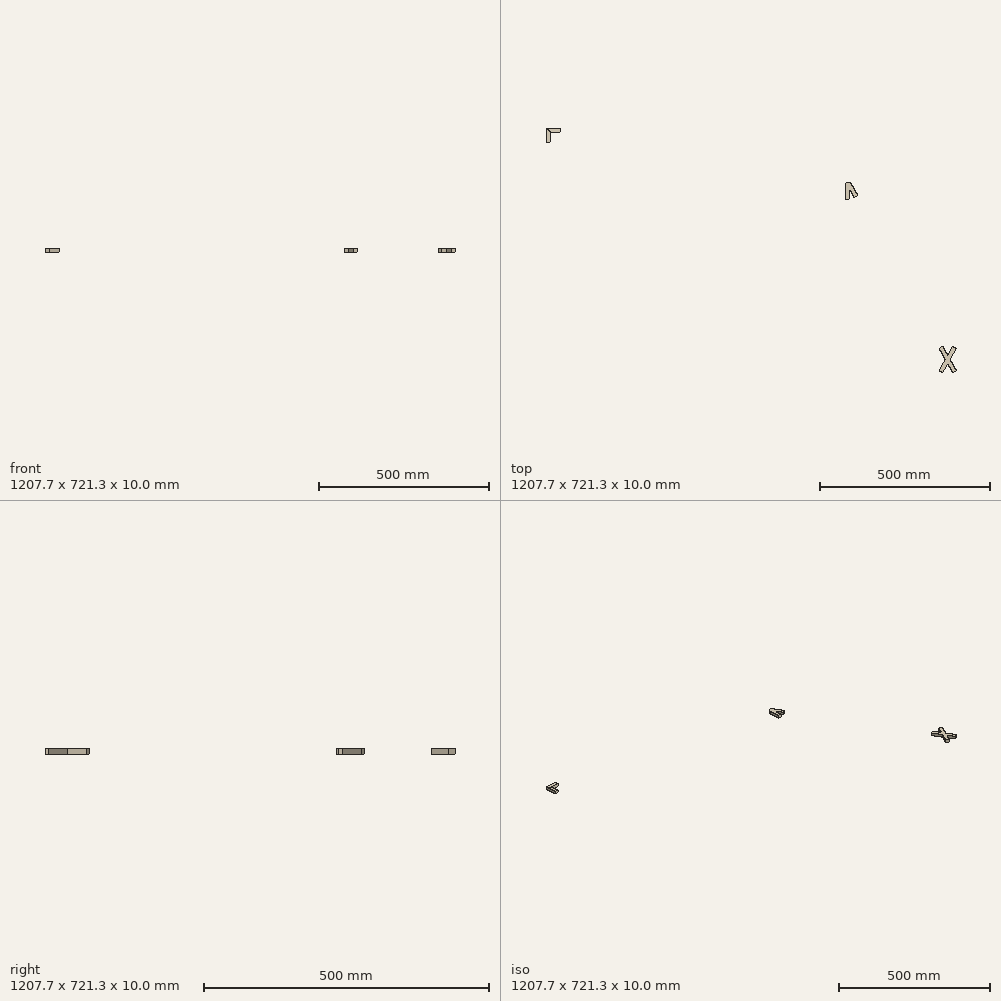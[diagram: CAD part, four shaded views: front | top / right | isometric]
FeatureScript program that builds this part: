
annotation { "Feature Type Name" : "Feature", "Feature Type Description" : "" }
export const myFeature = defineFeature(function(context is Context, id is Id, definition is map)
    precondition{}
    {
        {
            assignVariable(context, id + "F0", {"name" : "arm_height", "anyValue" : 10});
        }
        {
            var Q0;
            Q0=qCreatedBy(makeId("Top.planeOp"),FACE);
            var sketch = newSketch(context, id + "F1", { "sketchPlane" : qUnion([Q0])});
            skLineSegment(sketch, "E0.bottom", {"start": v(0, 0) * mm, "end": v(12.5, 0) * mm});
            skLineSegment(sketch, "E0.top", {"start": v(0, -1006) * mm, "end": v(12.5, -1006) * mm});
            skLineSegment(sketch, "E0.left", {"start": v(0, 0) * mm, "end": v(0, -1006) * mm});
            skLineSegment(sketch, "E0.right", {"start": v(12.5, 0) * mm, "end": v(12.5, -1006) * mm});
            skLineSegment(sketch, "E1.bottom", {"start": v(592.5, 0) * mm, "end": v(605, 0) * mm});
            skLineSegment(sketch, "E1.top", {"start": v(592.5, -1006) * mm, "end": v(605, -1006) * mm});
            skLineSegment(sketch, "E1.left", {"start": v(592.5, 0) * mm, "end": v(592.5, -1006) * mm});
            skLineSegment(sketch, "E1.right", {"start": v(605, 0) * mm, "end": v(605, -1006) * mm});
            skSolve(sketch);
        }
        {
            var Q0;
            Q0=qCreatedBy(makeId("Top.planeOp"),FACE);
            var sketch = newSketch(context, id + "F2", { "sketchPlane" : qUnion([Q0])});
            skLineSegment(sketch, "E2", {"start": v(0, -30) * mm, "end": v(0, 9.55) * mm});
            skLineSegment(sketch, "E3", {"start": v(18.72, 14.45) * mm, "end": v(38.1, -20.02) * mm});
            skLineSegment(sketch, "E4", {"start": v(38.1, -20.02) * mm, "end": v(27.2, -26.15) * mm});
            skLineSegment(sketch, "E5", {"start": v(27.2, -26.15) * mm, "end": v(12.5, 0) * mm});
            skLineSegment(sketch, "E6", {"start": v(12.5, 0) * mm, "end": v(12.5, -30) * mm});
            skLineSegment(sketch, "E7", {"start": v(12.5, -30) * mm, "end": v(0, -30) * mm});
            skLineSegment(sketch, "E8.0.0", {"start": v(0, 0) * mm, "end": v(0, -1006) * mm, "construction": true});
            skLineSegment(sketch, "E8.0.1", {"start": v(0, -1006) * mm, "end": v(12.5, -1006) * mm, "construction": true});
            skLineSegment(sketch, "E8.0.2", {"start": v(12.5, -1006) * mm, "end": v(12.5, 0) * mm, "construction": true});
            skLineSegment(sketch, "E8.0.3", {"start": v(12.5, 0) * mm, "end": v(0, 0) * mm, "construction": true});
            skLineSegment(sketch, "E9.0.0", {"start": v(592.5, 0) * mm, "end": v(592.5, -1006) * mm, "construction": true});
            skLineSegment(sketch, "E9.0.1", {"start": v(592.5, -1006) * mm, "end": v(605, -1006) * mm, "construction": true});
            skLineSegment(sketch, "E9.0.2", {"start": v(605, -1006) * mm, "end": v(605, 0) * mm, "construction": true});
            skLineSegment(sketch, "E9.0.3", {"start": v(605, 0) * mm, "end": v(592.5, 0) * mm, "construction": true});
            skLineSegment(sketch, "E10", {"start": v(12.5, 0) * mm, "end": v(581.6, -1012.13) * mm, "construction": true});
            skLineSegment(sketch, "E11", {"start": v(592.5, -1006) * mm, "end": v(23.4, 6.13) * mm, "construction": true});
            skLineSegment(sketch, "E12", {"start": v(23.4, 6.13) * mm, "end": v(12.5, 0) * mm, "construction": true});
            skLineSegment(sketch, "E13", {"start": v(581.6, -1012.13) * mm, "end": v(592.5, -1006) * mm, "construction": true});
            skLineSegment(sketch, "E14", {"start": v(592.5, 0) * mm, "end": v(12.5, 0) * mm, "construction": true});
            skPoint(sketch, "E15", {"position": v(302.5, 0) * mm});
            skLineSegment(sketch, "E16", {"start": v(302.5, 0) * mm, "end": v(302.5, -1006) * mm, "construction": true});
            skLineSegment(sketch, "E17.MirrorCS", {"start": v(23.4, -1012.13) * mm, "end": v(12.5, -1006) * mm, "construction": true});
            skLineSegment(sketch, "E18.MirrorCS", {"start": v(581.6, 6.13) * mm, "end": v(592.5, 0) * mm, "construction": true});
            skLineSegment(sketch, "E19.MirrorCS", {"start": v(592.5, 0) * mm, "end": v(23.4, -1012.13) * mm, "construction": true});
            skLineSegment(sketch, "E20.MirrorCS", {"start": v(12.5, -1006) * mm, "end": v(581.6, 6.13) * mm, "construction": true});
            skPoint(sketch, "E21.visualSharp", {"position": v(0, 47.73) * mm});
            skArc(sketch, "E21.filletArc", {"start": v(18.72, 14.45) * mm, "mid": v(7.47, 19.22) * mm, "end": v(0, 9.55) * mm});
            skSolve(sketch);
        }
        {
            var Q0;
            Q0=qCreatedBy(makeId("Top.planeOp"),FACE);
            var sketch = newSketch(context, id + "F3", { "sketchPlane" : qUnion([Q0])});
            skLineSegment(sketch, "E22.0", {"start": v(592.5, -1006) * mm, "end": v(23.4, 6.13) * mm, "construction": true});
            skLineSegment(sketch, "E23.0", {"start": v(12.5, 0) * mm, "end": v(581.6, -1012.13) * mm, "construction": true});
            skLineSegment(sketch, "E24.0", {"start": v(12.5, -1006) * mm, "end": v(581.6, 6.13) * mm, "construction": true});
            skLineSegment(sketch, "E25.0", {"start": v(592.5, 0) * mm, "end": v(23.4, -1012.13) * mm, "construction": true});
            skLineSegment(sketch, "E26", {"start": v(276.9, -470.22) * mm, "end": v(287.8, -464.1) * mm});
            skLineSegment(sketch, "E27", {"start": v(287.8, -464.1) * mm, "end": v(302.5, -490.25) * mm});
            skLineSegment(sketch, "E28", {"start": v(302.5, -490.25) * mm, "end": v(317.2, -464.1) * mm});
            skLineSegment(sketch, "E29", {"start": v(317.2, -464.1) * mm, "end": v(328.1, -470.22) * mm});
            skLineSegment(sketch, "E30", {"start": v(328.1, -470.22) * mm, "end": v(309.67, -503) * mm});
            skLineSegment(sketch, "E31", {"start": v(309.67, -503) * mm, "end": v(328.1, -535.78) * mm});
            skLineSegment(sketch, "E32", {"start": v(328.1, -535.78) * mm, "end": v(317.2, -541.9) * mm});
            skLineSegment(sketch, "E33", {"start": v(317.2, -541.9) * mm, "end": v(302.5, -515.75) * mm});
            skLineSegment(sketch, "E34", {"start": v(302.5, -515.75) * mm, "end": v(287.8, -541.9) * mm});
            skLineSegment(sketch, "E35", {"start": v(287.8, -541.9) * mm, "end": v(276.9, -535.78) * mm});
            skLineSegment(sketch, "E36", {"start": v(276.9, -535.78) * mm, "end": v(295.33, -503) * mm});
            skLineSegment(sketch, "E37", {"start": v(295.33, -503) * mm, "end": v(276.9, -470.22) * mm});
            skSolve(sketch);
        }
        {
            var Q0;
            Q0=makeQuery(id+"F2.imprint","IMPRINT",FACE,{"disambiguationData":[TD([[makeQuery(id+"F2.imprint","IMPRINT",EDGE,{"derivedFrom":sQuery(id+"F2.wireOp",EDGE,"E2")}),-1.0]])]});
            var Q1;
            Q1=makeQuery(id+"F3.imprint","IMPRINT",FACE,{"disambiguationData":[TD([[makeQuery(id+"F3.imprint","IMPRINT",EDGE,{"derivedFrom":sQuery(id+"F3.wireOp",EDGE,"E26")}),-1.0]])]});
            extrude(context, id + "F4", {"entities" : qUnion([Q0, Q1]), "depth" : (getVariable(context, 'arm_height')) * mm, "offsetDistance" : 25 * mm});
        }
        {
            var Q0;
            Q0=qCreatedBy(makeId("Top.planeOp"),FACE);
            var sketch = newSketch(context, id + "F5", { "sketchPlane" : qUnion([Q0])});
            skLineSegment(sketch, "E38", {"start": v(-879.62, 179.38) * mm, "end": v(-879.62, 136.88) * mm});
            skLineSegment(sketch, "E39", {"start": v(-879.62, 136.88) * mm, "end": v(-867.12, 136.88) * mm});
            skLineSegment(sketch, "E40", {"start": v(-867.12, 136.88) * mm, "end": v(-867.12, 166.88) * mm});
            skLineSegment(sketch, "E41", {"start": v(-867.12, 166.88) * mm, "end": v(-879.62, 179.38) * mm});
            skSolve(sketch);
        }
        {
            var Q0;
            Q0=makeQuery(id+"F5.imprint","IMPRINT",FACE,{"disambiguationData":[TD([[makeQuery(id+"F5.imprint","IMPRINT",EDGE,{"derivedFrom":sQuery(id+"F5.wireOp",EDGE,"E38")}),1.0]])]});
            extrude(context, id + "F6", {"entities" : qUnion([Q0]), "depth" : (getVariable(context, 'arm_height')) * mm, "offsetDistance" : 25 * mm});
        }
        {
            var Q0;
            Q0=makeQuery(id+"F6.opExtrude","SWEPT_BODY",BODY,{"disambiguationData":[OSD([sQuery(id+"F5.wireOp",EDGE,"E38"),sQuery(id+"F5.wireOp",EDGE,"E39"),sQuery(id+"F5.wireOp",EDGE,"E40"),sQuery(id+"F5.wireOp",EDGE,"E41")])]});
            var Q1;
            Q1=makeQuery(id+"F6.opExtrude","SWEPT_FACE",FACE,{"disambiguationData":[OSD([sQuery(id+"F5.wireOp",EDGE,"E41")])]});
            mirror(context, id + "F7", {"operationType" : NewBodyOperationType.ADD, "entities" : qUnion([Q0]), "mirrorPlane" : qUnion([Q1])});
        }
    });
